# Revit family: BalizadorConcreto_PBC9W-P_PBC9W-G_PowerLume
name_source: partatom
category: Luminárias
units: mm (PartAtom-declared; Revit-internal decimal feet)

## family parameters
Compartilhado = Sim
Corte com vazios quando carregada = Sim
Cota do conector redondo = Utilizar diâmetro
Fonte luminosa = Não
Hospedeiro = Face
Manter orientação da anotação = Não
Número OmniClass = 23.80.70.14.11.14
Ponto de cálculo do ambiente = Não
Tipo de parte = Normal
Título OmniClass = Post-Top Lighting

## types (2) — shared parameters
Carga Aparente Luminária = 0 VA
Catálogo de produtos = https://www.powerlume.com.br
Comentários de voltagem = 110 ou 220Vac 50/60Hz com driver incorporado
Contato do fabricante = (54) 3066-6488
Data da atualização = 27/02/2025
Descrição = Poste balizador LED em concreto
Difusor = PMMA transparente anti UV
Elevação-padrão = 1219 mm
Fabricante = Power Lume
Fator de Potência Luminária = 1
Fluxo luminoso = 760 lm
Frame = Concreto, leve
IP = 65
IRC = 90
IfcExportAs = IfcLightFixtureType
Largura = 150 mm
Localização = Caxias do Sul - RS / Brasil
Lâmpada = Placa LED
Peso = 0
Potência = 9W
Profundidade = 140 mm  [stored 0.459318 ft]
Temperatura de cor = 3000K
Tipo de imagem = pbc.1236.png
URL = https://www.powerlume.com.br
URL do produto = https://www.powerlume.com.br
Versão = 1
Vida útil = 60000h
Voltagem Luminária = 0 V
Ângulo de abertura = Difuso assimétrico

## per-type parameters (varying)
| type | Altura | Modelo de luminária |
| PBC9W-P | 456 mm  [stored 1.49606 ft] | BalizadorConcreto_PBC9W-P_Base_PowerLume : PBC9W-P |
| PBC9W-G | 750 mm  [stored 2.46063 ft] | BalizadorConcreto_PBC9W-G_Base_PowerLume : PBC9W-G |

note: column(s) folded — value = type name in every type: Modelo

note: [stored X ft] marks values corroborated as IEEE doubles in the binary element streams (Revit-internal decimal feet)
